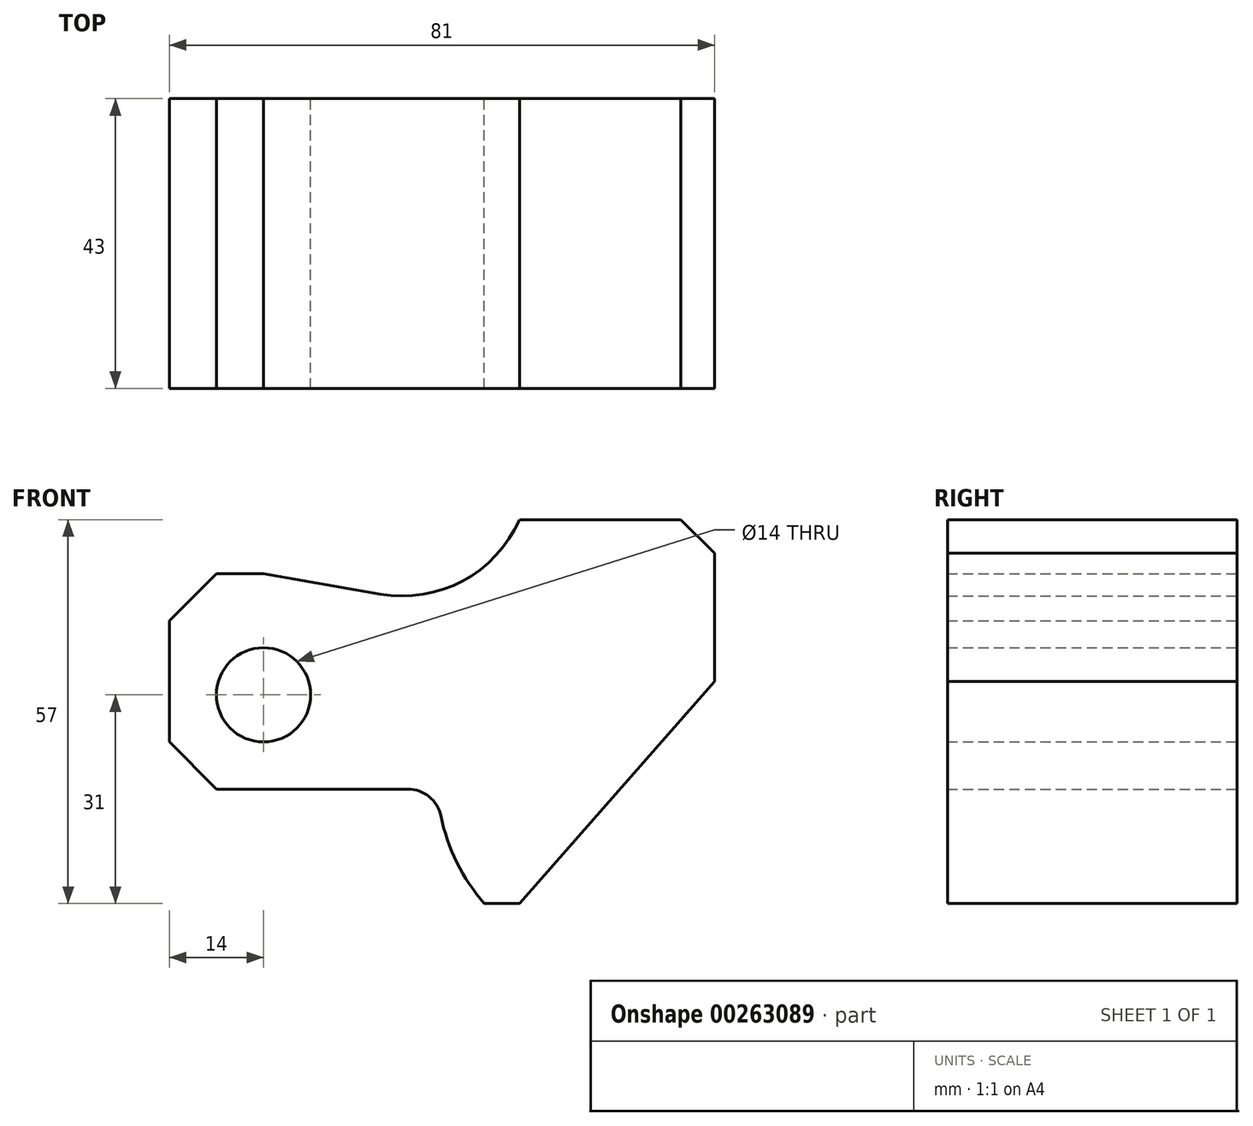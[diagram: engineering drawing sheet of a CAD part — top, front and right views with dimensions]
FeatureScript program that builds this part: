
annotation { "Feature Type Name" : "Feature", "Feature Type Description" : "" }
export const myFeature = defineFeature(function(context is Context, id is Id, definition is map)
    precondition{}
    {
        {
            var Q0;
            Q0=qCreatedBy(makeId("Front.planeOp"),FACE);
            var sketch = newSketch(context, id + "F0", { "sketchPlane" : qUnion([Q0])});
            skLineSegment(sketch, "E0", {"start": v(-26.5, 22.5) * mm, "end": v(-33.5, 22.5) * mm});
            skLineSegment(sketch, "E1", {"start": v(40.5, 25.5) * mm, "end": v(40.5, 6.5) * mm});
            skLineSegment(sketch, "E2", {"start": v(35.5, 30.5) * mm, "end": v(11.5, 30.5) * mm});
            skLineSegment(sketch, "E3", {"start": v(-0.73, -9.5) * mm, "end": v(-33.5, -9.5) * mm});
            skLineSegment(sketch, "E4", {"start": v(-40.5, 15.5) * mm, "end": v(-40.5, -2.5) * mm});
            skLineSegment(sketch, "E5", {"start": v(-26.5, 28.73) * mm, "end": v(-26.5, -23.4) * mm, "construction": true});
            skLineSegment(sketch, "E6", {"start": v(-53.87, 4.5) * mm, "end": v(-12.54, 4.5) * mm, "construction": true});
            skCircle(sketch, "E7", {"center": v(-26.5, 4.5) * mm, "radius": 7 * mm});
            skLineSegment(sketch, "E8", {"start": v(-40.5, -2.5) * mm, "end": v(-33.5, -9.5) * mm});
            skLineSegment(sketch, "E9", {"start": v(-40.5, 15.5) * mm, "end": v(-33.5, 22.5) * mm});
            skPoint(sketch, "E10.orphan", {"position": v(-40.5, 22.5) * mm});
            skPoint(sketch, "E11.second.point", {"position": v(-14.54, 52.93) * mm});
            skPoint(sketch, "E11.third.point", {"position": v(-15.3, 30.5) * mm});
            skLineSegment(sketch, "E12", {"start": v(-26.5, 22.5) * mm, "end": v(-9.19, 19.45) * mm});
            skArc(sketch, "E13", {"start": v(-9.19, 19.45) * mm, "mid": v(3.07, 21.4) * mm, "end": v(11.5, 30.5) * mm});
            skLineSegment(sketch, "E14", {"start": v(40.5, 25.5) * mm, "end": v(35.5, 30.5) * mm});
            skLineSegment(sketch, "E15", {"start": v(40.5, 6.5) * mm, "end": v(11.5, -26.5) * mm});
            skArc(sketch, "E16", {"start": v(6.29, -26.5) * mm, "mid": v(1.4, -18.57) * mm, "end": v(-0.73, -9.5) * mm});
            skLineSegment(sketch, "E17", {"start": v(11.5, -26.5) * mm, "end": v(6.29, -26.5) * mm});
            skSolve(sketch);
        }
        {
            var Q0;
            Q0=makeQuery(id+"F0.imprint","IMPRINT",FACE,{"disambiguationData":[TD([[makeQuery(id+"F0.imprint","IMPRINT",EDGE,{"derivedFrom":sQuery(id+"F0.wireOp",EDGE,"E0")}),1.0]])]});
            extrude(context, id + "F1", {"entities" : qUnion([Q0]), "depth" : 43 * mm, "symmetric" : true});
        }
        {
            var Q0;
            Q0=makeQuery(id+"F1.opExtrude","SWEPT_EDGE",EDGE,{"disambiguationData":[OSD([sQuery(id+"F0.wireOp",EDGE,"E3"),sQuery(id+"F0.wireOp",EDGE,"E16")])]});
            fillet(context, id + "F2", {"entities" : qUnion([Q0]), "radius" : 5 * mm, "tangentPropagation" : true, "allowEdgeOverflow" : false});
        }
    });
